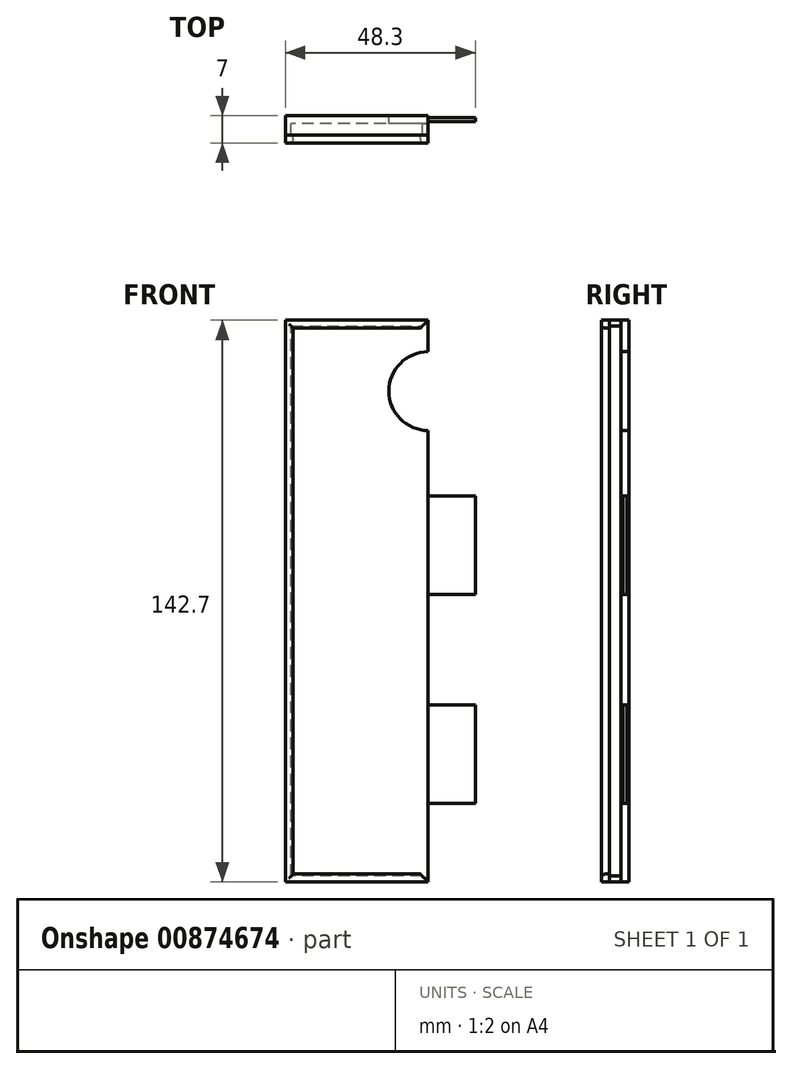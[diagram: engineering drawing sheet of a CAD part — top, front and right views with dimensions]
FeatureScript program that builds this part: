
annotation { "Feature Type Name" : "Feature", "Feature Type Description" : "" }
export const myFeature = defineFeature(function(context is Context, id is Id, definition is map)
    precondition{}
    {
        {
            var Q0;
            Q0=qCreatedBy(makeId("Front.planeOp"),FACE);
            var sketch = newSketch(context, id + "F0", { "sketchPlane" : qUnion([Q0])});
            skLineSegment(sketch, "E0.bottom", {"start": v(-34.1, 71.63) * mm, "end": v(2.2, 71.63) * mm});
            skLineSegment(sketch, "E0.top", {"start": v(-34.1, -71.07) * mm, "end": v(2.2, -71.07) * mm});
            skLineSegment(sketch, "E0.left", {"start": v(-34.1, 71.63) * mm, "end": v(-34.1, -71.07) * mm});
            skLineSegment(sketch, "E0.right", {"start": v(2.2, 71.63) * mm, "end": v(2.2, -71.07) * mm});
            skLineSegment(sketch, "E1.bottom", {"start": v(2.2, 26.93) * mm, "end": v(14.2, 26.93) * mm});
            skLineSegment(sketch, "E1.top", {"start": v(2.2, 1.93) * mm, "end": v(14.2, 1.93) * mm});
            skLineSegment(sketch, "E1.left", {"start": v(2.2, 26.93) * mm, "end": v(2.2, 1.93) * mm});
            skLineSegment(sketch, "E1.right", {"start": v(14.2, 26.93) * mm, "end": v(14.2, 1.93) * mm});
            skLineSegment(sketch, "E2.bottom", {"start": v(2.2, -26.07) * mm, "end": v(14.2, -26.07) * mm});
            skLineSegment(sketch, "E2.top", {"start": v(2.2, -51.07) * mm, "end": v(14.2, -51.07) * mm});
            skLineSegment(sketch, "E2.left", {"start": v(2.2, -26.07) * mm, "end": v(2.2, -51.07) * mm});
            skLineSegment(sketch, "E2.right", {"start": v(14.2, -26.07) * mm, "end": v(14.2, -51.07) * mm});
            skArc(sketch, "E3", {"start": v(2.2, 63.63) * mm, "mid": v(-7.8, 53.63) * mm, "end": v(2.2, 43.63) * mm});
            skPoint(sketch, "E3.first.point", {"position": v(2.2, 63.63) * mm});
            skPoint(sketch, "E3.second.point", {"position": v(2.2, 43.63) * mm});
            skPoint(sketch, "E3.third.point", {"position": v(12.03, 51.81) * mm});
            skSolve(sketch);
        }
        {
            var Q0;
            {var subQ1=sQuery(id+"F0.wireOp",EDGE,"E0.bottom");Q0=makeQuery(id+"F0.imprint","IMPRINT",FACE,{"disambiguationData":[TD([[makeQuery(id+"F0.imprint","IMPRINT",EDGE,{"derivedFrom":subQ1}),-1.0]])]});}
            extrude(context, id + "F1", {"entities" : qUnion([Q0]), "endBound" : BoundingType.SYMMETRIC, "depth" : 2 * mm, "offsetDistance" : 25 * mm});
        }
        {
            var Q0;
            Q0=makeQuery(id+"F0.imprint","IMPRINT",FACE,{"disambiguationData":[TD([[makeQuery(id+"F0.imprint","IMPRINT",EDGE,{"derivedFrom":sQuery(id+"F0.wireOp",EDGE,"E1.bottom")}),-1.0]])]});
            var Q1;
            Q1=makeQuery(id+"F0.imprint","IMPRINT",FACE,{"disambiguationData":[TD([[makeQuery(id+"F0.imprint","IMPRINT",EDGE,{"derivedFrom":sQuery(id+"F0.wireOp",EDGE,"E2.bottom")}),-1.0]])]});
            extrude(context, id + "F2", {"entities" : qUnion([Q0, Q1]), "operationType" : NewBodyOperationType.ADD, "endBound" : BoundingType.SYMMETRIC, "depth" : 1 * mm, "offsetDistance" : 25 * mm});
        }
        {
            var Q0;
            Q0=makeQuery(id+"F1.opExtrude","CAP_FACE",FACE,{"disambiguationData":[OSD([sQuery(id+"F0.wireOp",EDGE,"E0.bottom"),sQuery(id+"F0.wireOp",EDGE,"E0.top"),sQuery(id+"F0.wireOp",EDGE,"E0.left"),sQuery(id+"F0.wireOp",EDGE,"E0.right"),sQuery(id+"F0.wireOp",EDGE,"E1.left"),sQuery(id+"F0.wireOp",EDGE,"E2.left")])],"isStart":false});
            var sketch = newSketch(context, id + "F3", { "sketchPlane" : qUnion([Q0])});
            skLineSegment(sketch, "E4", {"start": v(2.2, -71.07) * mm, "end": v(-34.1, -71.07) * mm});
            skLineSegment(sketch, "E5", {"start": v(-34.1, -71.07) * mm, "end": v(-34.1, 71.63) * mm});
            skLineSegment(sketch, "E6", {"start": v(-34.1, 71.63) * mm, "end": v(2.2, 71.63) * mm});
            skLineSegment(sketch, "E7", {"start": v(0.7, -69.57) * mm, "end": v(-32.6, -69.57) * mm});
            skLineSegment(sketch, "E8", {"start": v(-32.6, -69.57) * mm, "end": v(-32.6, 70.13) * mm});
            skLineSegment(sketch, "E9", {"start": v(-32.6, 70.13) * mm, "end": v(0.7, 70.13) * mm});
            skLineSegment(sketch, "E10", {"start": v(0.7, 70.13) * mm, "end": v(2.2, 71.63) * mm});
            skLineSegment(sketch, "E11", {"start": v(0.7, -69.57) * mm, "end": v(2.2, -71.07) * mm});
            skSolve(sketch);
        }
        {
            var Q0;
            Q0 = qSketchRegion(id + "F3", true);
            extrude(context, id + "F4", {"entities" : qUnion([Q0]), "operationType" : NewBodyOperationType.ADD, "depth" : 3 * mm, "offsetDistance" : 25 * mm});
        }
        {
            var Q0;
            Q0=makeQuery(id+"F4.opExtrude","CAP_FACE",FACE,{"disambiguationData":[OSD([sQuery(id+"F3.wireOp",EDGE,"E4"),sQuery(id+"F3.wireOp",EDGE,"E5"),sQuery(id+"F3.wireOp",EDGE,"E6"),sQuery(id+"F3.wireOp",EDGE,"E7"),sQuery(id+"F3.wireOp",EDGE,"E8"),sQuery(id+"F3.wireOp",EDGE,"E9"),sQuery(id+"F3.wireOp",EDGE,"E10"),sQuery(id+"F3.wireOp",EDGE,"E11")])],"isStart":false});
            var sketch = newSketch(context, id + "F5", { "sketchPlane" : qUnion([Q0])});
            skLineSegment(sketch, "E12", {"start": v(2.2, -71.07) * mm, "end": v(-34.1, -71.07) * mm});
            skLineSegment(sketch, "E13", {"start": v(-34.1, -71.07) * mm, "end": v(-34.1, 71.63) * mm});
            skLineSegment(sketch, "E14", {"start": v(-34.1, 71.63) * mm, "end": v(2.2, 71.63) * mm});
            skLineSegment(sketch, "E15", {"start": v(2.2, -71.07) * mm, "end": v(0.2, -69.07) * mm});
            skLineSegment(sketch, "E16", {"start": v(2.2, 71.63) * mm, "end": v(0.2, 69.63) * mm});
            skLineSegment(sketch, "E17", {"start": v(0.2, 69.63) * mm, "end": v(-32.1, 69.63) * mm});
            skLineSegment(sketch, "E18", {"start": v(-32.1, 69.63) * mm, "end": v(-32.1, -69.07) * mm});
            skLineSegment(sketch, "E19", {"start": v(-32.1, -69.07) * mm, "end": v(0.2, -69.07) * mm});
            skLineSegment(sketch, "E20", {"start": v(1.2, -70.07) * mm, "end": v(-33.1, -70.07) * mm});
            skLineSegment(sketch, "E21", {"start": v(-33.1, -70.07) * mm, "end": v(-33.1, 70.63) * mm});
            skLineSegment(sketch, "E22", {"start": v(1.2, 70.63) * mm, "end": v(-33.1, 70.63) * mm});
            skSolve(sketch);
        }
        {
            var Q0;
            Q0 = qSketchRegion(id + "F5", true);
            extrude(context, id + "F6", {"entities" : qUnion([Q0]), "depth" : 2 * mm, "offsetDistance" : 25 * mm});
        }
        {
            var Q0;
            Q0=makeQuery(id+"F6.opExtrude","CAP_EDGE",EDGE,{"disambiguationData":[OSD([sQuery(id+"F5.wireOp",EDGE,"E18")])],"isStart":false});
            var Q1;
            Q1=makeQuery(id+"F6.opExtrude","CAP_EDGE",EDGE,{"disambiguationData":[OSD([sQuery(id+"F5.wireOp",EDGE,"E17")])],"isStart":false});
            var Q2;
            Q2=makeQuery(id+"F6.opExtrude","CAP_EDGE",EDGE,{"disambiguationData":[OSD([sQuery(id+"F5.wireOp",EDGE,"E19")])],"isStart":false});
            fillet(context, id + "F7", {"entities" : qUnion([Q0, Q1, Q2]), "radius" : 1 * mm, "tangentPropagation" : true, "allowEdgeOverflow" : false});
        }
    });
